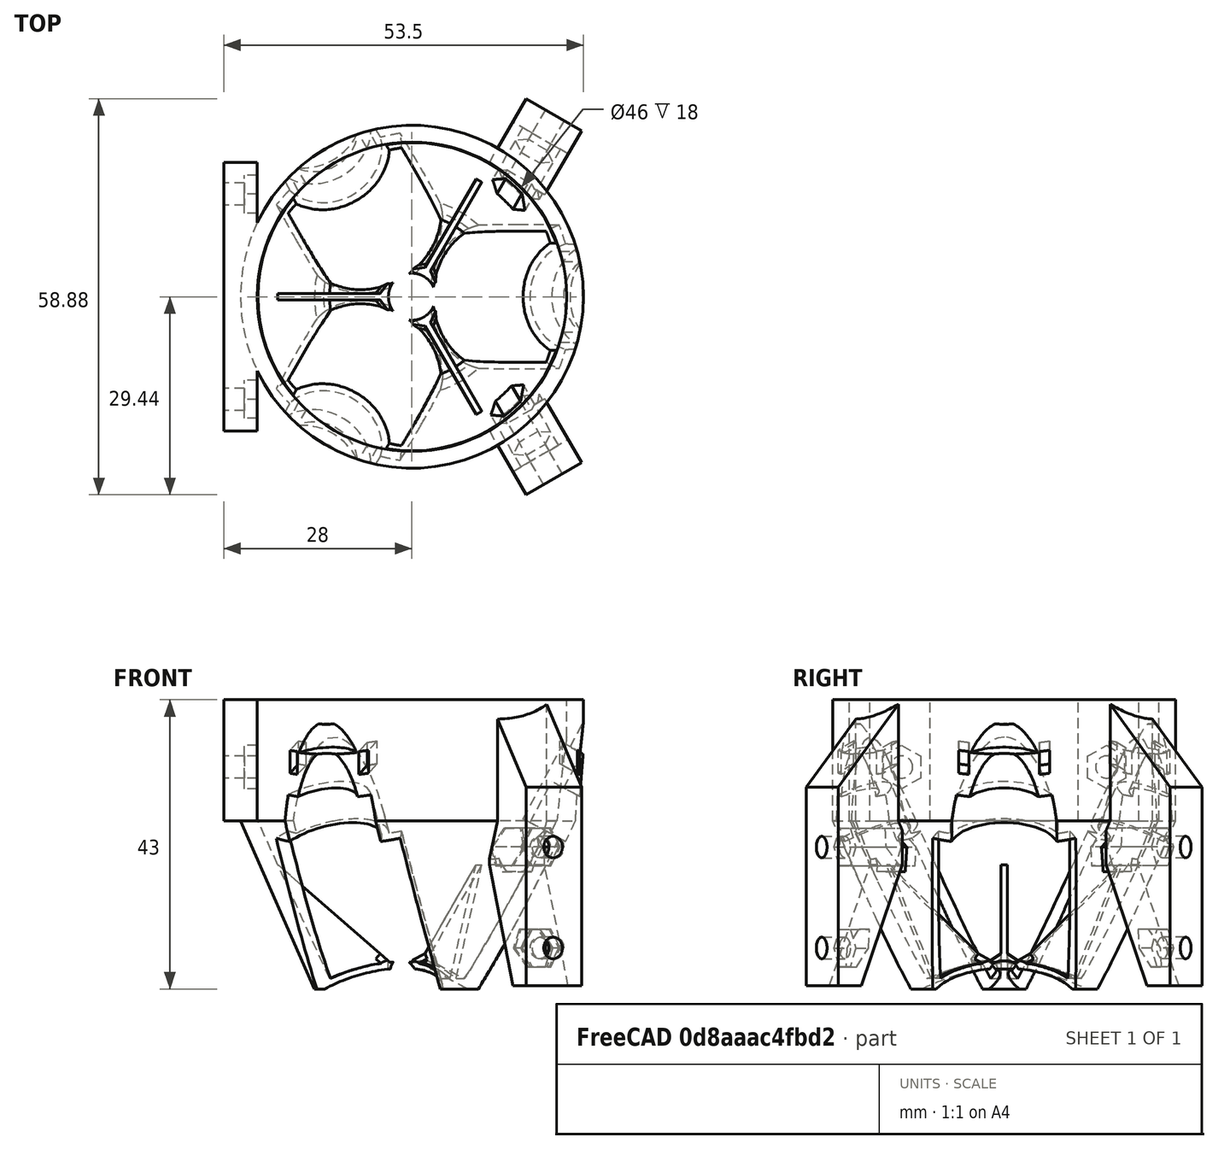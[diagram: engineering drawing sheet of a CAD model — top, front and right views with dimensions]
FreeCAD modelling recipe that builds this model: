
FCSTD DOCUMENT  (FreeCAD 0.19R)
Label: hotend-diamond-blower
License: All rights reserved
LicenseURL: http://en.wikipedia.org/wiki/All_rights_reserved
objects: Part::Cylinder×30, Part::Fuse×23, Part::Box×17, Part::MultiFuse×12, Part::Prism×8, Part::Cut×7, Part::Cone×2, Part::Sphere×2, Part::FeaturePython×2, PartDesign::FeatureBase×1, PartDesign::Body×1
note: 105 computed .brp shape members not serialized (recipe doc carries the construction recipe); baked Part::Feature solids carry a one-line shape summary decoded from their .brp

FEATURE [Part::Cone] cylinder
  Angle = 360
  AttacherType = Attacher::AttachEngine3D
  Height = 25
  Radius1 = 14.5
  Radius2 = 25.5
FEATURE [Part::Prism] prism
  AttacherType = Attacher::AttachEngine3D
  Circumradius = 4.225
  FirstAngle = 0
  Height = 20
  Placement = pos=(20.7435,26.1288,46.6) rot=(0.186157,0.694747,-0.694747;3.50969rad)
  Polygon = 6
  SecondAngle = 0
FEATURE [Part::Prism] prism001
  AttacherType = Attacher::AttachEngine3D
  Circumradius = 4.225
  FirstAngle = 0
  Height = 20
  Placement = pos=(10.7435,-8.80833,46.6) rot=(-0.186157,0.694747,-0.694747;2.77349rad)
  Polygon = 6
  SecondAngle = 0
FEATURE [Part::Fuse] Matrix_Union
  Base = -> prism
  Placement = pos=(0,0,-25.5) rot=(0,0,1;0rad)
  Tool = -> prism001
FEATURE [Part::Fuse] union
  Base = -> cylinder
  Tool = -> Matrix_Union
FEATURE [Part::Sphere] sphere
  Angle1 = -90
  Angle2 = 90
  Angle3 = 360
  AttacherType = Attacher::AttachEngine3D
  Placement = pos=(0,0,-25.49) rot=(0,0,1;0rad)
  Radius = 28.6923
FEATURE [Part::Cylinder] cylinder001
  Angle = 360
  AttacherType = Attacher::AttachEngine3D
  Height = 2.39233
  Placement = pos=(0,0,2.19233) rot=(0,0,1;0rad)
  Radius = 3.5
FEATURE [Part::Cone] cylinder002
  Angle = 360
  AttacherType = Attacher::AttachEngine3D
  Height = 24.2
  Radius1 = 12
  Radius2 = 23
FEATURE [Part::Cylinder] cylinder003
  Angle = 360
  AttacherType = Attacher::AttachEngine3D
  Height = 17.75
  Placement = pos=(24.6003,0,46.2665) rot=(0,1,0;0.488692rad)
  Radius = 9.25
FEATURE [Part::Cylinder] cylinder004
  Angle = 360
  AttacherType = Attacher::AttachEngine3D
  Height = 17.75
  Placement = pos=(-12.3002,21.3045,46.2665) rot=(-0.239596,0.138331,0.960967;2.12853rad)
  Radius = 9.25
FEATURE [Part::Cylinder] cylinder005
  Angle = 360
  AttacherType = Attacher::AttachEngine3D
  Height = 17.75
  Placement = pos=(-12.3002,-21.3045,46.2665) rot=(-0.239596,-0.138331,0.960967;4.15466rad)
  Radius = 9.25
FEATURE [Part::MultiFuse] Group
  Placement = pos=(0,0,-26.49) rot=(0,0,1;0rad)
  Shapes = -> [cylinder003,cylinder004,cylinder005]
FEATURE [Part::Sphere] sphere001
  Angle1 = -90
  Angle2 = 90
  Angle3 = 360
  AttacherType = Attacher::AttachEngine3D
  Placement = pos=(0,0,-26.49) rot=(0,0,1;0rad)
  Radius = 29.6923
FEATURE [Part::Fuse] union001
  Base = -> Group
  Tool = -> sphere001
FEATURE [Part::Cut] difference
  Base = -> cylinder002
  Tool = -> union001
FEATURE [Part::Box] cube
  AttacherType = Attacher::AttachEngine3D
  Height = 100
  Length = 10
  Placement = pos=(0,0.5,0) rot=(0,0,1;3.14159rad)
  Width = 1
FEATURE [Part::Box] cube001
  AttacherType = Attacher::AttachEngine3D
  Height = 1
  Length = 3
  Placement = pos=(5e-16,2e-16,-2.12132) rot=(0.357407,-0.862856,-0.357407;1.71777rad)
  Width = 3
FEATURE [Part::Fuse] union002
  Base = -> cube
  Placement = pos=(-3.5,0,0) rot=(0,-1,0;0.855211rad)
  Tool = -> cube001
FEATURE [Part::Box] cube002
  AttacherType = Attacher::AttachEngine3D
  Height = 100
  Length = 10
  Placement = pos=(0,0.5,0) rot=(0,0,1;3.14159rad)
  Width = 1
FEATURE [Part::Box] cube003
  AttacherType = Attacher::AttachEngine3D
  Height = 1
  Length = 3
  Placement = pos=(5e-16,2e-16,-2.12132) rot=(0.357407,-0.862856,-0.357407;1.71777rad)
  Width = 3
FEATURE [Part::Fuse] union003
  Base = -> cube002
  Placement = pos=(1.75,-3.03109,0) rot=(0.403295,-0.232843,0.88495;2.19689rad)
  Tool = -> cube003
FEATURE [Part::Box] cube004
  AttacherType = Attacher::AttachEngine3D
  Height = 100
  Length = 10
  Placement = pos=(0,0.5,0) rot=(0,0,1;3.14159rad)
  Width = 1
FEATURE [Part::Box] cube005
  AttacherType = Attacher::AttachEngine3D
  Height = 1
  Length = 3
  Placement = pos=(5e-16,2e-16,-2.12132) rot=(0.357407,-0.862856,-0.357407;1.71777rad)
  Width = 3
FEATURE [Part::Fuse] union004
  Base = -> cube004
  Placement = pos=(1.75,3.03109,0) rot=(0.403295,0.232843,0.88495;4.08629rad)
  Tool = -> cube005
FEATURE [Part::MultiFuse] Group001
  Placement = pos=(0,0,3.19233) rot=(0,0,1;0rad)
  Shapes = -> [union002,union003,union004]
FEATURE [Part::Cut] difference001
  Base = -> difference
  Placement = pos=(0,0,1) rot=(0,0,1;0rad)
  Tool = -> Group001
FEATURE [Part::MultiFuse] union005
  Placement = pos=(0,0,-0.01) rot=(0,0,1;0rad)
  Shapes = -> [sphere,cylinder001,difference001]
FEATURE [Part::Cut] difference002
  Base = -> union
  Placement = pos=(0,0,25.5) rot=(0,0,1;0rad)
  Tool = -> union005
FEATURE [Part::Cylinder] cylinder006
  Angle = 360
  AttacherType = Attacher::AttachEngine3D
  Height = 18
  Placement = pos=(0,0,50.5) rot=(0,0,1;0rad)
  Radius = 25.5
FEATURE [Part::Cylinder] cylinder007
  Angle = 360
  AttacherType = Attacher::AttachEngine3D
  Height = 20
  Placement = pos=(0,0,49.5) rot=(0,0,1;0rad)
  Radius = 23
FEATURE [Part::Cylinder] cylinder008
  Angle = 360
  AttacherType = Attacher::AttachEngine3D
  Height = 17.75
  Placement = pos=(24.6003,0,46.2665) rot=(0,1,0;0.488692rad)
  Radius = 9.25
FEATURE [Part::Cylinder] cylinder009
  Angle = 360
  AttacherType = Attacher::AttachEngine3D
  Height = 17.75
  Placement = pos=(-12.3002,21.3045,46.2665) rot=(-0.239596,0.138331,0.960967;2.12853rad)
  Radius = 9.25
FEATURE [Part::Cylinder] cylinder010
  Angle = 360
  AttacherType = Attacher::AttachEngine3D
  Height = 17.75
  Placement = pos=(-12.3002,-21.3045,46.2665) rot=(-0.239596,-0.138331,0.960967;4.15466rad)
  Radius = 9.25
FEATURE [Part::MultiFuse] Group002
  Shapes = -> [cylinder008,cylinder009,cylinder010]
FEATURE [Part::Cut] difference003
  Base = -> cylinder007
  Tool = -> Group002
FEATURE [Part::Cut] difference004
  Base = -> cylinder006
  Tool = -> difference003
FEATURE [Part::Box] cube006
  AttacherType = Attacher::AttachEngine3D
  Height = 18
  Length = 5
  Placement = pos=(-5,-20,-18) rot=(0,0,1;0rad)
  Width = 40
FEATURE [Part::Cylinder] cylinder011
  Angle = 360
  AttacherType = Attacher::AttachEngine3D
  Height = 6
  Radius = 1.65
FEATURE [Part::Prism] prism002
  AttacherType = Attacher::AttachEngine3D
  Circumradius = 3.25
  FirstAngle = 0
  Height = 2
  Polygon = 6
  SecondAngle = 0
FEATURE [Part::Fuse] union006
  Base = -> cylinder011
  Placement = pos=(0.1,-15.25,-10) rot=(0,-1,0;1.5708rad)
  Tool = -> prism002
FEATURE [Part::Cylinder] cylinder012
  Angle = 360
  AttacherType = Attacher::AttachEngine3D
  Height = 6
  Radius = 1.65
FEATURE [Part::Prism] prism003
  AttacherType = Attacher::AttachEngine3D
  Circumradius = 3.25
  FirstAngle = 0
  Height = 2
  Polygon = 6
  SecondAngle = 0
FEATURE [Part::Fuse] union007
  Base = -> cylinder012
  Placement = pos=(0.1,15.25,-10) rot=(0,-1,0;1.5708rad)
  Tool = -> prism003
FEATURE [Part::Fuse] Group003
  Base = -> union006
  Tool = -> union007
FEATURE [Part::Cut] difference005
  Base = -> cube006
  Placement = pos=(-23,0,68.5) rot=(0,0,1;0rad)
  Tool = -> Group003
FEATURE [Part::Box] cube007
  AttacherType = Attacher::AttachEngine3D
  Height = 29.5
  Length = 9.5
  Width = 4
FEATURE [Part::Box] cube008
  AttacherType = Attacher::AttachEngine3D
  Height = 24.5
  Length = 9.5
  Placement = pos=(0,10.9,18) rot=(0,0,1;0rad)
  Width = 0.1
FEATURE [Part::FeaturePython] hull  # WARN: FeaturePython — macro-defined, semantics opaque (R4)
  Arguments = []
  Children = -> [cube007,cube008]
  Operation = hull
  Placement = pos=(25.2272,24.6949,26) rot=(0,0,1;2.61799rad)
FEATURE [Part::Box] cube009
  AttacherType = Attacher::AttachEngine3D
  Height = 29.5
  Length = 9.5
  Width = 4
FEATURE [Part::Box] cube010
  AttacherType = Attacher::AttachEngine3D
  Height = 24.5
  Length = 9.5
  Placement = pos=(0,10.9,18) rot=(0,0,1;0rad)
  Width = 0.1
FEATURE [Part::FeaturePython] hull001  # WARN: FeaturePython — macro-defined, semantics opaque (R4)
  Arguments = []
  Children = -> [cube009,cube010]
  Operation = hull
  Placement = pos=(17,-29.4449,26) rot=(0,0,-1;5.75959rad)
FEATURE [Part::MultiFuse] union008
  Shapes = -> [difference002,difference004,difference005,hull,hull001]
FEATURE [Part::Cylinder] cylinder013
  Angle = 360
  AttacherType = Attacher::AttachEngine3D
  Height = 26.2
  Radius = 11.1
FEATURE [Part::Cylinder] cylinder014
  Angle = 360
  AttacherType = Attacher::AttachEngine3D
  Height = 8.1
  Placement = pos=(0,0,-1) rot=(0,0,1;0rad)
  Radius = 8.1
FEATURE [Part::Cylinder] cylinder015
  Angle = 360
  AttacherType = Attacher::AttachEngine3D
  Height = 8
  Placement = pos=(0,0,-1) rot=(0,0,1;0rad)
  Radius = 6.1
FEATURE [Part::Cylinder] cylinder016
  Angle = 360
  AttacherType = Attacher::AttachEngine3D
  Height = 3.95
  Placement = pos=(0,0,5.9) rot=(0,0,1;0rad)
  Radius = 8.1
FEATURE [Part::Box] cube011
  AttacherType = Attacher::AttachEngine3D
  Height = 3.01
  Length = 16
  Placement = pos=(-16,-6.75,2.995) rot=(0,0,1;0rad)
  Width = 1.5
FEATURE [Part::Box] cube012
  AttacherType = Attacher::AttachEngine3D
  Height = 3.01
  Length = 16
  Placement = pos=(-16,5.25,2.995) rot=(0,0,1;0rad)
  Width = 1.5
FEATURE [Part::Fuse] Group004
  Base = -> cube011
  Tool = -> cube012
FEATURE [Part::MultiFuse] union009
  Placement = pos=(0,0,7) rot=(0,0,1;0rad)
  Shapes = -> [cylinder015,cylinder016,Group004]
FEATURE [Part::Fuse] union010
  Base = -> cylinder014
  Placement = pos=(0,0,26) rot=(0,0,1;0rad)
  Tool = -> union009
FEATURE [Part::Cylinder] cylinder017
  Angle = 360
  AttacherType = Attacher::AttachEngine3D
  Height = 4
  Placement = pos=(0,0,0) rot=(1,0,0;3.14159rad)
  Radius = 3
FEATURE [Part::MultiFuse] union011
  Placement = pos=(12.394,0,23.3098) rot=(0,1,0;0.488692rad)
  Shapes = -> [cylinder013,union010,cylinder017]
FEATURE [Part::Cylinder] cylinder018
  Angle = 360
  AttacherType = Attacher::AttachEngine3D
  Height = 26.2
  Radius = 11.1
FEATURE [Part::Cylinder] cylinder019
  Angle = 360
  AttacherType = Attacher::AttachEngine3D
  Height = 8.1
  Placement = pos=(0,0,-1) rot=(0,0,1;0rad)
  Radius = 8.1
FEATURE [Part::Cylinder] cylinder020
  Angle = 360
  AttacherType = Attacher::AttachEngine3D
  Height = 8
  Placement = pos=(0,0,-1) rot=(0,0,1;0rad)
  Radius = 6.1
FEATURE [Part::Cylinder] cylinder021
  Angle = 360
  AttacherType = Attacher::AttachEngine3D
  Height = 3.95
  Placement = pos=(0,0,5.9) rot=(0,0,1;0rad)
  Radius = 8.1
FEATURE [Part::Box] cube013
  AttacherType = Attacher::AttachEngine3D
  Height = 3.01
  Length = 16
  Placement = pos=(-16,-6.75,2.995) rot=(0,0,1;0rad)
  Width = 1.5
FEATURE [Part::Box] cube014
  AttacherType = Attacher::AttachEngine3D
  Height = 3.01
  Length = 16
  Placement = pos=(-16,5.25,2.995) rot=(0,0,1;0rad)
  Width = 1.5
FEATURE [Part::Fuse] Group005
  Base = -> cube013
  Tool = -> cube014
FEATURE [Part::MultiFuse] union012
  Placement = pos=(0,0,7) rot=(0,0,1;0rad)
  Shapes = -> [cylinder020,cylinder021,Group005]
FEATURE [Part::Fuse] union013
  Base = -> cylinder019
  Placement = pos=(0,0,26) rot=(0,0,1;0rad)
  Tool = -> union012
FEATURE [Part::Cylinder] cylinder022
  Angle = 360
  AttacherType = Attacher::AttachEngine3D
  Height = 4
  Placement = pos=(0,0,0) rot=(1,0,0;3.14159rad)
  Radius = 3
FEATURE [Part::MultiFuse] union014
  Placement = pos=(-6.19702,10.7336,23.3098) rot=(-0.239596,0.138331,0.960967;2.12853rad)
  Shapes = -> [cylinder018,union013,cylinder022]
FEATURE [Part::Cylinder] cylinder023
  Angle = 360
  AttacherType = Attacher::AttachEngine3D
  Height = 26.2
  Radius = 11.1
FEATURE [Part::Cylinder] cylinder024
  Angle = 360
  AttacherType = Attacher::AttachEngine3D
  Height = 8.1
  Placement = pos=(0,0,-1) rot=(0,0,1;0rad)
  Radius = 8.1
FEATURE [Part::Cylinder] cylinder025
  Angle = 360
  AttacherType = Attacher::AttachEngine3D
  Height = 8
  Placement = pos=(0,0,-1) rot=(0,0,1;0rad)
  Radius = 6.1
FEATURE [Part::Cylinder] cylinder026
  Angle = 360
  AttacherType = Attacher::AttachEngine3D
  Height = 3.95
  Placement = pos=(0,0,5.9) rot=(0,0,1;0rad)
  Radius = 8.1
FEATURE [Part::Box] cube015
  AttacherType = Attacher::AttachEngine3D
  Height = 3.01
  Length = 16
  Placement = pos=(-16,-6.75,2.995) rot=(0,0,1;0rad)
  Width = 1.5
FEATURE [Part::Box] cube016
  AttacherType = Attacher::AttachEngine3D
  Height = 3.01
  Length = 16
  Placement = pos=(-16,5.25,2.995) rot=(0,0,1;0rad)
  Width = 1.5
FEATURE [Part::Fuse] Group006
  Base = -> cube015
  Tool = -> cube016
FEATURE [Part::MultiFuse] union015
  Placement = pos=(0,0,7) rot=(0,0,1;0rad)
  Shapes = -> [cylinder025,cylinder026,Group006]
FEATURE [Part::Fuse] union016
  Base = -> cylinder024
  Placement = pos=(0,0,26) rot=(0,0,1;0rad)
  Tool = -> union015
FEATURE [Part::Cylinder] cylinder027
  Angle = 360
  AttacherType = Attacher::AttachEngine3D
  Height = 4
  Placement = pos=(0,0,0) rot=(1,0,0;3.14159rad)
  Radius = 3
FEATURE [Part::MultiFuse] union017
  Placement = pos=(-6.19702,-10.7336,23.3098) rot=(-0.239596,-0.138331,0.960967;4.15466rad)
  Shapes = -> [cylinder023,union016,cylinder027]
FEATURE [Part::MultiFuse] Group007
  Shapes = -> [union011,union014,union017]
FEATURE [Part::Cylinder] cylinder028
  Angle = 360
  AttacherType = Attacher::AttachEngine3D
  Height = 10
  Radius = 1.6
FEATURE [Part::Prism] prism004
  AttacherType = Attacher::AttachEngine3D
  Circumradius = 3.225
  FirstAngle = 0
  Height = 22
  Placement = pos=(0,0,4) rot=(0,0,1;0rad)
  Polygon = 6
  SecondAngle = 0
FEATURE [Part::Fuse] union018
  Base = -> cylinder028
  Placement = pos=(-21,-5,0) rot=(1,0,0;3.14159rad)
  Tool = -> prism004
FEATURE [Part::Cylinder] cylinder029
  Angle = 360
  AttacherType = Attacher::AttachEngine3D
  Height = 10
  Radius = 1.6
FEATURE [Part::Prism] prism005
  AttacherType = Attacher::AttachEngine3D
  Circumradius = 3.225
  FirstAngle = 0
  Height = 7
  Placement = pos=(0,0,4) rot=(0,0,1;0rad)
  Polygon = 6
  SecondAngle = 0
FEATURE [Part::Fuse] union019
  Base = -> cylinder029
  Placement = pos=(-21,-20,0) rot=(1,0,0;3.14159rad)
  Tool = -> prism005
FEATURE [Part::Fuse] Group008
  Base = -> union018
  Placement = pos=(3.06199,37.5035,51.6) rot=(0.186157,0.694747,0.694747;2.77349rad)
  Tool = -> union019
FEATURE [Part::Cylinder] cylinder030
  Angle = 360
  AttacherType = Attacher::AttachEngine3D
  Height = 10
  Radius = 1.6
FEATURE [Part::Prism] prism006
  AttacherType = Attacher::AttachEngine3D
  Circumradius = 3.225
  FirstAngle = 0
  Height = 22
  Placement = pos=(0,0,4) rot=(0,0,1;0rad)
  Polygon = 6
  SecondAngle = 0
FEATURE [Part::Fuse] union020
  Base = -> cylinder030
  Placement = pos=(-21,-5,0) rot=(1,0,0;3.14159rad)
  Tool = -> prism006
FEATURE [Part::Cylinder] cylinder031
  Angle = 360
  AttacherType = Attacher::AttachEngine3D
  Height = 10
  Radius = 1.6
FEATURE [Part::Prism] prism007
  AttacherType = Attacher::AttachEngine3D
  Circumradius = 3.225
  FirstAngle = 0
  Height = 7
  Placement = pos=(0,0,4) rot=(0,0,1;0rad)
  Polygon = 6
  SecondAngle = 0
FEATURE [Part::Fuse] union021
  Base = -> cylinder031
  Placement = pos=(-21,-20,0) rot=(1,0,0;3.14159rad)
  Tool = -> prism007
FEATURE [Part::Fuse] Group009
  Base = -> union020
  Placement = pos=(39.1753,-16.6535,51.6) rot=(-0.935113,-0.250563,-0.250563;4.64535rad)
  Tool = -> union021
FEATURE [Part::Fuse] Group010
  Base = -> Group008
  Tool = -> Group009
FEATURE [Part::Fuse] union022
  Base = -> Group007
  Tool = -> Group010
FEATURE [Part::Cut] difference006
  Base = -> union008
  Placement = pos=(0,8.4e-15,68.5) rot=(1,0,0;3.14159rad)
  Refine = true
  Tool = -> union022
FEATURE [PartDesign::FeatureBase] BaseFeature
  BaseFeature = -> difference006
FEATURE [PartDesign::Body] Body
  BaseFeature = -> difference006
  Group = -> [BaseFeature]
  Origin = -> Origin
  Tip = -> BaseFeature
